FCSTD DOCUMENT  (FreeCAD 0.16R6704 (Git))
Label: hexpiece
License: All rights reserved
LicenseURL: http://en.wikipedia.org/wiki/All_rights_reserved
objects: Sketcher::SketchObject×1
note: 1 computed .brp shape members not serialized (recipe doc carries the construction recipe); baked Part::Feature solids carry a one-line shape summary decoded from their .brp

FEATURE [Sketcher::SketchObject] Sketch
  sketch-geometry (9):
    g0: LineSegment StartX=-5 StartY=-8.66025 StartZ=0 EndX=5 EndY=-8.66025 EndZ=0
    g1: LineSegment StartX=5 StartY=-8.66025 StartZ=0 EndX=10 EndY=0 EndZ=0
    g2: LineSegment StartX=10 StartY=0 StartZ=0 EndX=5 EndY=8.66025 EndZ=0
    g3: LineSegment StartX=5 StartY=8.66025 StartZ=0 EndX=-5 EndY=8.66025 EndZ=0
    g4: LineSegment StartX=-5 StartY=8.66025 StartZ=0 EndX=-10 EndY=0 EndZ=0
    g5: LineSegment StartX=-10 StartY=0 StartZ=0 EndX=-5 EndY=-8.66025 EndZ=0
    g6: LineSegment [constr] StartX=-5 StartY=-8.66025 StartZ=0 EndX=5 EndY=8.66025 EndZ=0
    g7: LineSegment [constr] StartX=-5 StartY=8.66025 StartZ=0 EndX=5 EndY=-8.66025 EndZ=0
    g8: Circle CenterX=0 CenterY=0 CenterZ=0 NormalX=0 NormalY=0 NormalZ=1 Radius=5
  constraints (24):
    c: Horizontal(g0)
    c: Coincident(g0,g1)
    c: Coincident(g1,g2)
    c: Coincident(g2,g3)
    c: Coincident(g3,g4)
    c: Coincident(g4,g5)
    c: Equal(g2,g3)
    c: Equal(g3,g4)
    c: Equal(g4,g5)
    c: Equal(g5,g0)
    c: Equal(g0,g1)
    c: Angle(g4,g3) = 2.0944
    c: Angle(g2,g1) = 2.0944
    c: Angle(g0,g5) = 2.0944
    c: Coincident(g6,g2)
    c: Coincident(g7,g3)
    c: Coincident(g7,g0)
    c: Coincident(g5,g0)
    c: Coincident(g5,g6)
    c: PointOnObject(g-1,g7)
    c: PointOnObject(g-1,g6)
    c: Coincident(g8,g-1)
    c: DistanceX(g3,g3) = 10
    c: Radius(g8) = 5
